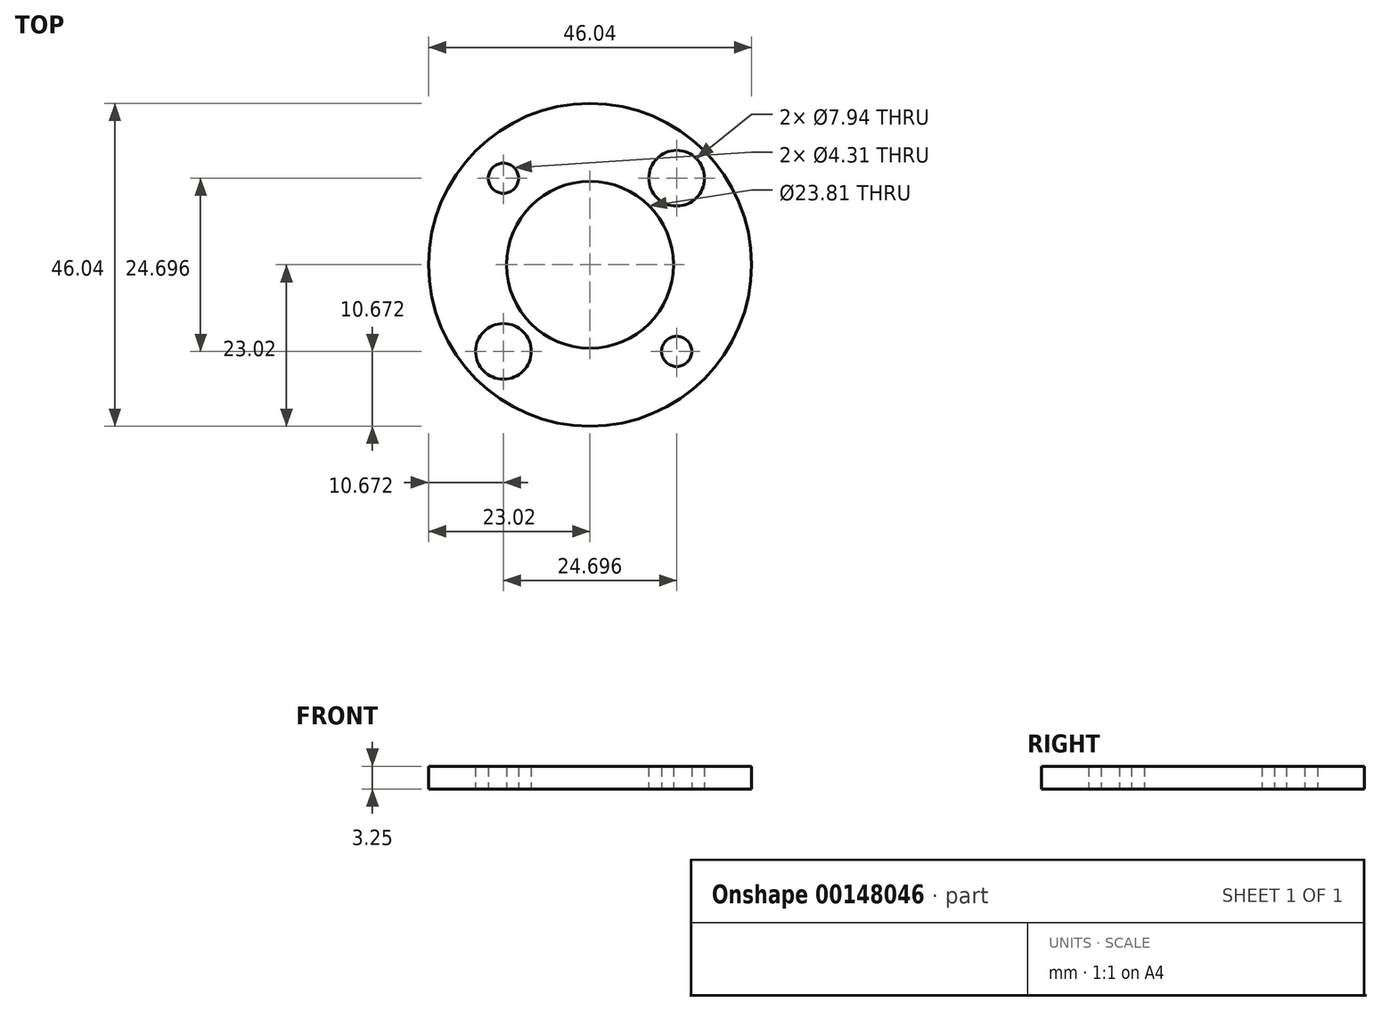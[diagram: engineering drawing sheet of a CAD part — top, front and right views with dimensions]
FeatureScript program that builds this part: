
annotation { "Feature Type Name" : "Feature", "Feature Type Description" : "" }
export const myFeature = defineFeature(function(context is Context, id is Id, definition is map)
    precondition{}
    {
        {
            var Q0;
            Q0=qCreatedBy(makeId("Top.planeOp"),FACE);
            var sketch = newSketch(context, id + "F0", { "sketchPlane" : qUnion([Q0])});
            skCircle(sketch, "E0", {"center": v(0, 0) * mm, "radius": 23.02 * mm});
            skCircle(sketch, "E1", {"center": v(0, 0) * mm, "radius": 11.9 * mm});
            skLineSegment(sketch, "E2.bottom", {"start": v(-12.35, 12.35) * mm, "end": v(12.35, 12.35) * mm, "construction": true});
            skLineSegment(sketch, "E2.top", {"start": v(-12.35, -12.35) * mm, "end": v(12.35, -12.35) * mm, "construction": true});
            skLineSegment(sketch, "E2.left", {"start": v(-12.35, 12.35) * mm, "end": v(-12.35, -12.35) * mm, "construction": true});
            skLineSegment(sketch, "E2.right", {"start": v(12.35, 12.35) * mm, "end": v(12.35, -12.35) * mm, "construction": true});
            skCircle(sketch, "E3", {"center": v(-12.35, 12.35) * mm, "radius": 5.56 * mm, "construction": true});
            skCircle(sketch, "E4", {"center": v(12.35, 12.35) * mm, "radius": 3.97 * mm});
            skCircle(sketch, "E5", {"center": v(-12.35, 12.35) * mm, "radius": 2.15 * mm});
            skCircle(sketch, "E6", {"center": v(-12.35, -12.35) * mm, "radius": 3.97 * mm});
            skCircle(sketch, "E7", {"center": v(12.35, -12.35) * mm, "radius": 2.15 * mm});
            skSolve(sketch);
        }
        {
            var Q0;
            Q0=qSketchRegion(id+"F0",true);
            extrude(context, id + "F1", {"entities" : qUnion([Q0]), "depth" : 3.25 * mm});
        }
    });
